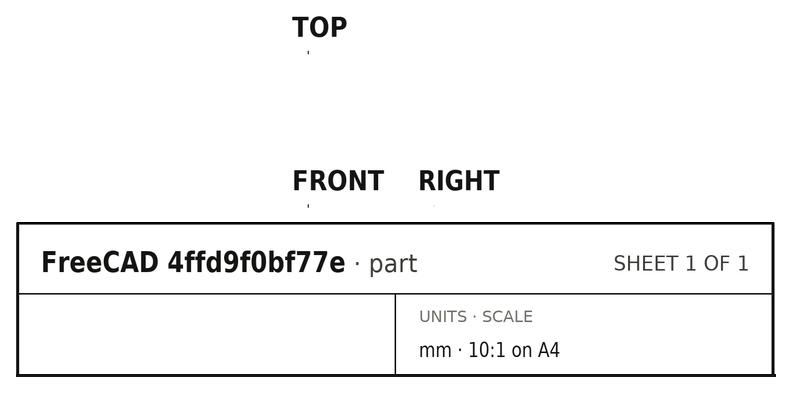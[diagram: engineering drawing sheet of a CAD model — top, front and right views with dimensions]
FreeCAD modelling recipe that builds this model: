
FCSTD DOCUMENT  (FreeCAD 0.19R)
Label: Lee_microstrip
License: All rights reserved
LicenseURL: http://en.wikipedia.org/wiki/All_rights_reserved
objects: Part::Part2DObjectPython×5, App::FeaturePython×2, Part::Cut×1, Part::FeaturePython×1
note: 7 computed .brp shape members not serialized (recipe doc carries the construction recipe); baked Part::Feature solids carry a one-line shape summary decoded from their .brp

FEATURE [Part::Part2DObjectPython] Line  label="_PV1"  # Draft 2D object (typed FeaturePython)
  Area = 0
  ChamferSize = 0
  Closed = false
  End = (0.00125,0.00025,0)
  FilletRadius = 0
  Length = 0.00025
  MakeFace = true
  Placement = pos=(0.0025,0,0) rot=(0,0,1;0rad)
  Points = (2) [(-0.00125,3.82702e-20,0),(-0.00125,0.00025,0)]
  Start = (0.00125,0,0)
  Subdivisions = 0
FEATURE [Part::Part2DObjectPython] Rectangle004  label="Lee_semiconductor"  # Draft 2D object (typed FeaturePython)
  Area = 6.25e-07
  ChamferSize = 0
  Columns = 1
  FilletRadius = 0
  Height = 0.00025
  Length = 0.0025
  MakeFace = true
  Rows = 1
FEATURE [Part::Part2DObjectPython] Rectangle005  label="strip001"  # Draft 2D object (typed FeaturePython)
  Area = 1.25e-08
  ChamferSize = 0
  Columns = 1
  FilletRadius = 0
  Height = 5e-05
  Length = 0.00025
  MakeFace = true
  Placement = pos=(0.001125,0.00025,0) rot=(0,0,1;0rad)
  Rows = 1
FEATURE [Part::Part2DObjectPython] Rectangle006  label="air001"  # Draft 2D object (typed FeaturePython)
  Area = 5.625e-06
  ChamferSize = 0
  Columns = 1
  FilletRadius = 0
  Height = 0.00225
  Length = 0.0025
  MakeFace = true
  Placement = pos=(0,0.00025,0) rot=(0,0,1;0rad)
  Rows = 1
FEATURE [Part::Cut] Cut001  label="air002"
  Base = -> Rectangle006
  Tool = -> Rectangle005
FEATURE [Part::FeaturePython] BooleanFragments001  label="Lee_microstrip"  # WARN: FeaturePython — macro-defined, semantics opaque (R4)
  Mode = 0
  Objects = -> [Rectangle004,Cut001]
  Tolerance = 0
FEATURE [Part::Part2DObjectPython] Rectangle  label="_Pline1"  # Draft 2D object (typed FeaturePython)
  Area = 0
  ChamferSize = 0
  Columns = 1
  FilletRadius = 0
  Height = 5e-05
  Length = 0.00025
  MakeFace = false
  Placement = pos=(0.001125,0.00025,0) rot=(0,0,1;0rad)
  Rows = 1
FEATURE [App::FeaturePython] Text  label="_M1(voltage){V1}"  # WARN: FeaturePython — macro-defined, semantics opaque (R4)
  Placement = pos=(0.00123975,-0.000526531,0) rot=(0,0,1;0rad)
  Text = .
FEATURE [App::FeaturePython] Text001  label="_M1(current){line1}"  # WARN: FeaturePython — macro-defined, semantics opaque (R4)
  Placement = pos=(0.00123975,-0.000526531,0) rot=(0,0,1;0rad)
  Text = .
